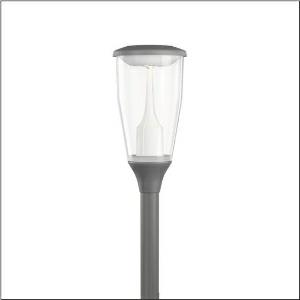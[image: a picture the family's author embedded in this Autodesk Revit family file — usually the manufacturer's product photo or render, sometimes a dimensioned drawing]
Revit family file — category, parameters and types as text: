
# Revit family: dl_11_iq___p1_0a_5xa5565ff14hp00022_87ad
name_source: partatom
category: Lighting Fixtures
units: mm (PartAtom-declared; Revit-internal decimal feet)

## family parameters
Cut with Voids When Loaded = No
Host = Face
Light Source = No
Part Type = Normal
Room Calculation Point = No
Round Connector Dimension = Use Diameter
Shared = No

## types (1)
- --- (1 x LED, 4780 lm, 33.6 W, 3000K)
    Apparent Load = 34 VA
    CIE Flux Codes = 33 63 91 94 100
    Color Rendering = 70
    Color Temperature = 3000K
    Default Elevation = 1800 mm
    Description = DL 11 iQ, mast luminaire, Module 540 iQ-SR, primary light control with 3 zone facetted reflector, of plastic, silver coated, highly specular, structured, primary optical cover: cover, of PMMA, transparent, light distribution: P1.0a, light emission: direct distribution, primary light characteristic: asymmetric, installation type: post-top, LED, High Power LED, light colour: 730, colour temperature: 3000K, control gear: iQ Street-Remote, control: Street-Remote, Auto-Match, Temp-Guard, Lumen-Switch, Night-Set, Smart-Wire, Light-Fading, Desk-Remote (wireless, voltage-free reading and setting of iQ features in the workshop via application-optimized NFC function/RFID function), optimised constant luminous flux control (CLO 2.0), mains connection: 220..240V, AC, 50/60Hz, connection cable pre-assembled, cable length: 5,5m, start of lifetime: 34W, end of service life: 36W, luminaire housing, upper part, of diecast aluminium, coated, Siteco® metallic grey (DB 702S), spigot size: 60mm (post-top), mounting height: 3..5m, post-top mast mounting element, of diecast aluminium, coated, Siteco® metallic grey (DB 702S), Module 540 iQ-SR, traffic white (RAL 9016), equipment: Power, protection rating (complete): IP66, insulation class (complete): insulation class II (safety insulation), certification: CE, ENEC, ENEC+, VDE, impact resistance: IK07, packaging unit: 1 piece

Light Distribution: P1.0a
    Height = 665 mm
    Lamp = 1 x LED
    Lamp Light Flux = 4780 lm
    Lamp Power = 33.6 W
    Lamp count = 1
    Length = 334 mm
    Luminous efficacy = 142 lm/W
    Manufacturer = Siteco
    ModVariant = No
    Model = 5XA5565FF14HP00022
    Number of Poles = 1
    OnlyDefault = Yes
    Power Factor = 1
    Product Name = DL 11 iQ | P1.0a
    Product group = mast luminaire | pylon top
    ProductGroupID = 6100
    Protection Class = Protection class II
    Protection Degree = IP 66
    RLX_Detail_Level = 1
    RLX_Emergency_Light_Flux = 0 lm
    RLX_Emergency_Type = 0
    RLX_Emergency_Type_DB = No
    RlxData = <blob elided: 105117 chars, md5=c13ce8d5>
    Socket = socket
    Standby Power = 0 W
    System Light Flux = 4780 lm
    System Power = 34 W
    Type Comments = factory setting: luminous flux: 100 % | dim-lin: 254 | 695 mA
    Type Image = l_1258354.jpg
    URL = http://relux.com
    VarID = @adj_033398
    Voltage = 0 V
    Weight = 0.00 kg
    Width = 0 mm  [stored 0 ft]

note: [stored X ft] marks values corroborated as IEEE doubles in the binary element streams (Revit-internal decimal feet)

## geometry (parser evidence)
native form markers: Blend x4, Sweep x9
no freeform markers — native parametric forms only
